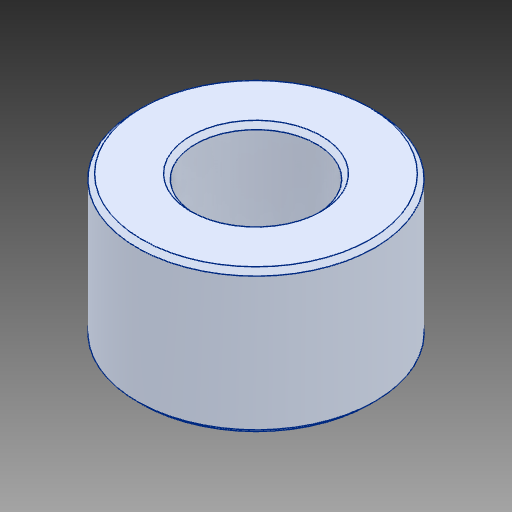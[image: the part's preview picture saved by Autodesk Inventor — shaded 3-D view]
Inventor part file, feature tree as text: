
AUTODESK INVENTOR PART (.ipt)
format: ipt  version: 2017 (Build 210142000, 142)  size: 112,640 bytes
history: mixed  units: mm
features: chamfer x1, imported_body x1
ambient origin geometry x8: Origin, YZ Plane, XZ Plane, XY Plane, X Axis, Y Axis, Z Axis, Center Point
bodies: Solid1 (imported_parasolid)
feature tree (2):
  chamfer  "Chamfer1"  [1 undecoded]
  imported_body  NMx_Import_Brep_tag  [imported B-rep: ~8 faces, bbox_mm=[2.45, 0.0, 6.0]]
note: 1 required parameter value undecoded (feature->parameter linkage not recoverable at this tier; creation-order binding heuristic only, values carry confidence <= 0.55)
